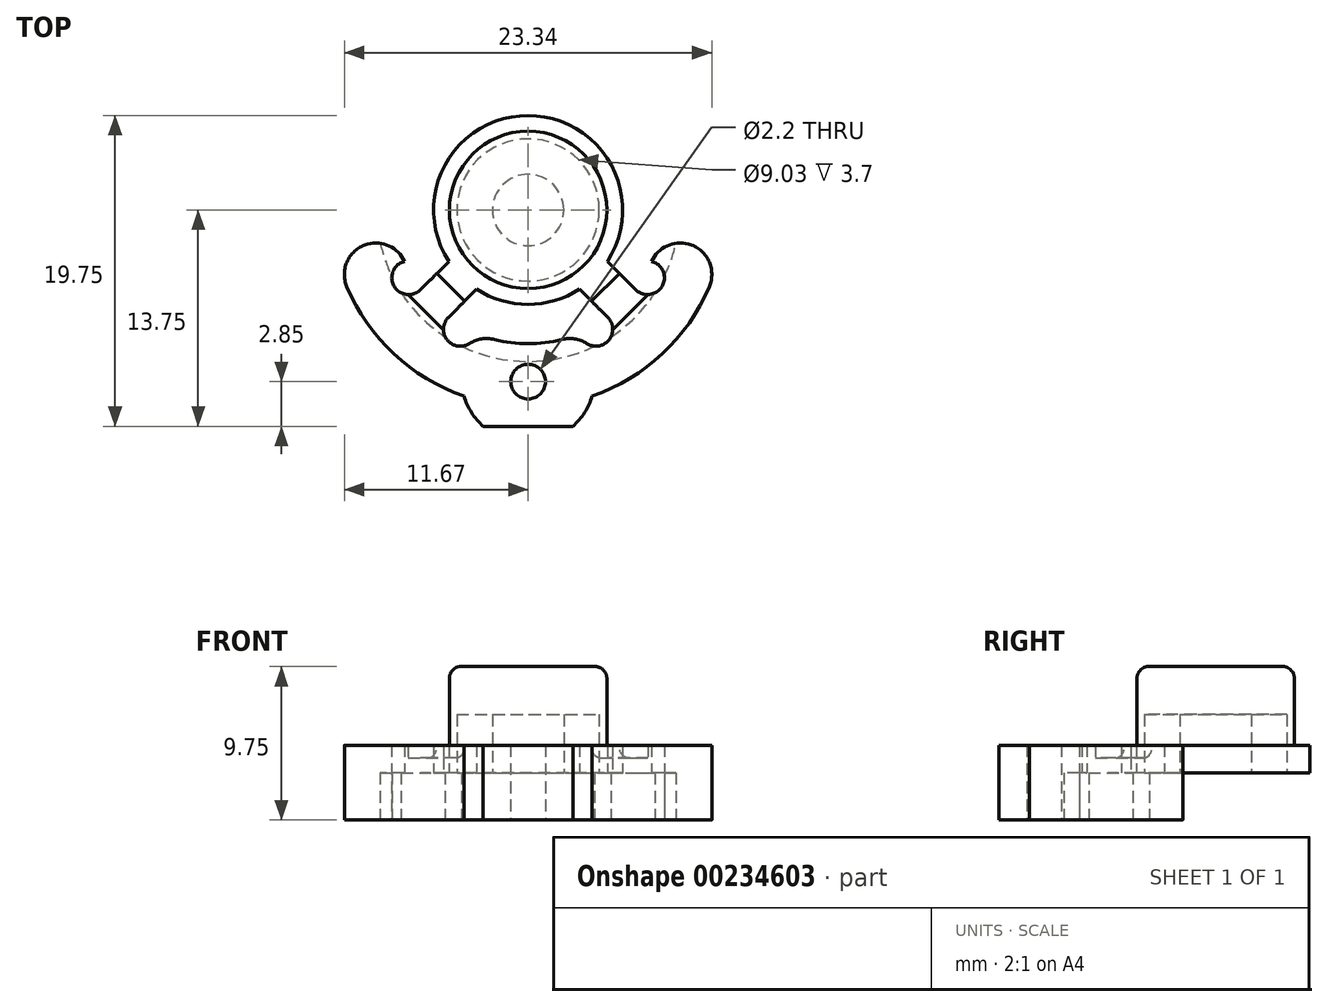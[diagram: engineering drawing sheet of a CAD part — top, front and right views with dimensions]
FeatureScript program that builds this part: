
annotation { "Feature Type Name" : "Feature", "Feature Type Description" : "" }
export const myFeature = defineFeature(function(context is Context, id is Id, definition is map)
    precondition{}
    {
        {
            var Q0;
            Q0=qCreatedBy(makeId("Top.planeOp"),FACE);
            var sketch = newSketch(context, id + "F0", { "sketchPlane" : qUnion([Q0])});
            skLineSegment(sketch, "E0.bottom", {"start": v(4, 3) * mm, "end": v(-4, 3) * mm, "construction": true});
            skLineSegment(sketch, "E0.top", {"start": v(4, -3) * mm, "end": v(-4, -3) * mm, "construction": true});
            skLineSegment(sketch, "E0.left", {"start": v(4, 3) * mm, "end": v(4, -3) * mm, "construction": true});
            skLineSegment(sketch, "E0.right", {"start": v(-4, 3) * mm, "end": v(-4, -3) * mm, "construction": true});
            skPoint(sketch, "E0.middle", {"position": v(0, 0) * mm});
            skArc(sketch, "E1", {"start": v(-12.2, -2.7) * mm, "mid": v(-9.33, -8.32) * mm, "end": v(-4.08, -11.82) * mm});
            skArc(sketch, "E2.converted", {"start": v(-3.27, -5.03) * mm, "mid": v(0, -6) * mm, "end": v(3.27, -5.03) * mm});
            skArc(sketch, "E3", {"start": v(-8.34, -1.67) * mm, "mid": v(-8.13, -2.48) * mm, "end": v(-7.85, -3.27) * mm});
            skPoint(sketch, "E4.orphan", {"position": v(-6, 0) * mm});
            skLineSegment(sketch, "E5", {"start": v(0, 0) * mm, "end": v(14.62, -14.62) * mm, "construction": true});
            skLineSegment(sketch, "E6", {"start": v(5.03, -3.27) * mm, "end": v(6.83, -5.06) * mm});
            skLineSegment(sketch, "E7.MirrorCS", {"start": v(3.27, -5.03) * mm, "end": v(5.06, -6.83) * mm});
            skLineSegment(sketch, "E8.MirrorCS", {"start": v(-5.03, -3.27) * mm, "end": v(-6.83, -5.06) * mm});
            skLineSegment(sketch, "E9.MirrorCS", {"start": v(-3.27, -5.03) * mm, "end": v(-5.06, -6.83) * mm});
            skArc(sketch, "E10", {"start": v(6.83, -5.06) * mm, "mid": v(8.52, -4.83) * mm, "end": v(7.85, -3.27) * mm});
            skArc(sketch, "E11.MirrorCS", {"start": v(5.06, -6.83) * mm, "mid": v(4.83, -8.52) * mm, "end": v(3.27, -7.85) * mm});
            skArc(sketch, "E12.trimOffspring", {"start": v(7.85, -3.27) * mm, "mid": v(8.13, -2.48) * mm, "end": v(8.34, -1.67) * mm});
            skArc(sketch, "E13.MirrorCS", {"start": v(-5.06, -6.83) * mm, "mid": v(-4.83, -8.52) * mm, "end": v(-3.27, -7.85) * mm});
            skArc(sketch, "E14.MirrorCS", {"start": v(-6.83, -5.06) * mm, "mid": v(-8.52, -4.83) * mm, "end": v(-7.85, -3.27) * mm});
            skArc(sketch, "E15.trimOffspring", {"start": v(-3.27, -7.85) * mm, "mid": v(0, -8.5) * mm, "end": v(3.27, -7.85) * mm});
            skArc(sketch, "E16.trimOffspring", {"start": v(5.03, -3.27) * mm, "mid": v(0, 6) * mm, "end": v(-5.03, -3.27) * mm});
            skArc(sketch, "E17.trimOffspring", {"start": v(4.08, -11.82) * mm, "mid": v(9.33, -8.32) * mm, "end": v(12.2, -2.7) * mm});
            skArc(sketch, "E18.trimOffspring", {"start": v(-4.08, -11.82) * mm, "mid": v(-3.6, -12.87) * mm, "end": v(-2.85, -13.75) * mm});
            skCircle(sketch, "E19", {"center": v(0, -10.9) * mm, "radius": 1.1 * mm});
            skLineSegment(sketch, "E20", {"start": v(-8.34, -1.67) * mm, "end": v(-12.2, -2.7) * mm});
            skLineSegment(sketch, "E21.MirrorCS", {"start": v(8.34, -1.67) * mm, "end": v(12.2, -2.7) * mm});
            skPoint(sketch, "E22.orphan", {"position": v(-13.8, -3.13) * mm});
            skPoint(sketch, "E23.orphan", {"position": v(12.5, 0) * mm});
            skPoint(sketch, "E24.orphan", {"position": v(13.8, -3.13) * mm});
            skLineSegment(sketch, "E25", {"start": v(-2.85, -13.75) * mm, "end": v(2.85, -13.75) * mm});
            skArc(sketch, "E26.trimOffspring", {"start": v(2.85, -13.75) * mm, "mid": v(3.6, -12.87) * mm, "end": v(4.08, -11.82) * mm});
            skSolve(sketch);
        }
        {
            var Q0;
            Q0 = qSketchRegion(id + "F0", true);
            extrude(context, id + "F1", {"entities" : qUnion([Q0]), "depth" : 4.75 * mm});
        }
        {
            var Q0;
            Q0=makeQuery(id+"F1.opExtrude","CAP_FACE",FACE,{"disambiguationData":[OSD([sQuery(id+"F0.wireOp",EDGE,"E1"),sQuery(id+"F0.wireOp",EDGE,"E2.converted"),sQuery(id+"F0.wireOp",EDGE,"rdbc6vYB-NVjA-jXWY-TLaR-nZ7SSUkQD9Vy"),sQuery(id+"F0.wireOp",EDGE,"ynKpnGIP-DJsh-uGPF-F4s2-QlGlmaUKXdbb"),sQuery(id+"F0.wireOp",EDGE,"E3"),sQuery(id+"F0.wireOp",EDGE,"E6"),sQuery(id+"F0.wireOp",EDGE,"E7.MirrorCS"),sQuery(id+"F0.wireOp",EDGE,"E8.MirrorCS"),sQuery(id+"F0.wireOp",EDGE,"E9.MirrorCS"),sQuery(id+"F0.wireOp",EDGE,"E10"),sQuery(id+"F0.wireOp",EDGE,"E11.MirrorCS"),sQuery(id+"F0.wireOp",EDGE,"E12.trimOffspring"),sQuery(id+"F0.wireOp",EDGE,"E13.MirrorCS"),sQuery(id+"F0.wireOp",EDGE,"E14.MirrorCS"),sQuery(id+"F0.wireOp",EDGE,"E15.trimOffspring"),sQuery(id+"F0.wireOp",EDGE,"E16.trimOffspring")])],"isStart":false});
            var sketch = newSketch(context, id + "F2", { "sketchPlane" : qUnion([Q0])});
            skCircle(sketch, "E27", {"center": v(0, 0) * mm, "radius": 5 * mm});
            skSolve(sketch);
        }
        {
            var Q0;
            Q0=makeQuery(id+"F2.imprint","IMPRINT",FACE,{"disambiguationData":[TD([[makeQuery(id+"F2.imprint","IMPRINT",EDGE,{"derivedFrom":sQuery(id+"F2.wireOp",EDGE,"E27")}),1.0]])]});
            extrude(context, id + "F3", {"entities" : qUnion([Q0]), "operationType" : NewBodyOperationType.ADD, "depth" : 5 * mm});
        }
        {
            var Q0;
            Q0=makeQuery(id+"F1.opExtrude","CAP_FACE",FACE,{"disambiguationData":[OSD([sQuery(id+"F0.wireOp",EDGE,"E1"),sQuery(id+"F0.wireOp",EDGE,"E2.converted"),sQuery(id+"F0.wireOp",EDGE,"rdbc6vYB-NVjA-jXWY-TLaR-nZ7SSUkQD9Vy"),sQuery(id+"F0.wireOp",EDGE,"ynKpnGIP-DJsh-uGPF-F4s2-QlGlmaUKXdbb"),sQuery(id+"F0.wireOp",EDGE,"E3"),sQuery(id+"F0.wireOp",EDGE,"E6"),sQuery(id+"F0.wireOp",EDGE,"E7.MirrorCS"),sQuery(id+"F0.wireOp",EDGE,"E8.MirrorCS"),sQuery(id+"F0.wireOp",EDGE,"E9.MirrorCS"),sQuery(id+"F0.wireOp",EDGE,"E10"),sQuery(id+"F0.wireOp",EDGE,"E11.MirrorCS"),sQuery(id+"F0.wireOp",EDGE,"E12.trimOffspring"),sQuery(id+"F0.wireOp",EDGE,"E13.MirrorCS"),sQuery(id+"F0.wireOp",EDGE,"E14.MirrorCS"),sQuery(id+"F0.wireOp",EDGE,"E15.trimOffspring"),sQuery(id+"F0.wireOp",EDGE,"E16.trimOffspring")])],"isStart":false});
            var sketch = newSketch(context, id + "F4", { "sketchPlane" : qUnion([Q0])});
            skSolve(sketch);
        }
        {
            var Q0;
            Q0=makeQuery(id+"F1.opExtrude","SWEPT_EDGE",EDGE,{"disambiguationData":[OSD([sQuery(id+"F0.wireOp",EDGE,"E17.trimOffspring"),sQuery(id+"F0.wireOp",EDGE,"E21.MirrorCS")])]});
            var Q1;
            Q1=makeQuery(id+"F1.opExtrude","SWEPT_EDGE",EDGE,{"disambiguationData":[OSD([sQuery(id+"F0.wireOp",EDGE,"E12.trimOffspring"),sQuery(id+"F0.wireOp",EDGE,"E21.MirrorCS")])]});
            var Q2;
            Q2=makeQuery(id+"F1.opExtrude","SWEPT_EDGE",EDGE,{"disambiguationData":[OSD([sQuery(id+"F0.wireOp",EDGE,"E3"),sQuery(id+"F0.wireOp",EDGE,"E20")])]});
            var Q3;
            Q3=makeQuery(id+"F1.opExtrude","SWEPT_EDGE",EDGE,{"disambiguationData":[OSD([sQuery(id+"F0.wireOp",EDGE,"E1"),sQuery(id+"F0.wireOp",EDGE,"E20")])]});
            var Q4;
            Q4=makeQuery(id+"F1.opExtrude","SWEPT_EDGE",EDGE,{"disambiguationData":[OSD([sQuery(id+"F0.wireOp",EDGE,"E11.MirrorCS"),sQuery(id+"F0.wireOp",EDGE,"E15.trimOffspring")])]});
            var Q5;
            Q5=makeQuery(id+"F1.opExtrude","SWEPT_EDGE",EDGE,{"disambiguationData":[OSD([sQuery(id+"F0.wireOp",EDGE,"E13.MirrorCS"),sQuery(id+"F0.wireOp",EDGE,"E15.trimOffspring")])]});
            fillet(context, id + "F5", {"entities" : qUnion([Q0, Q1, Q2, Q3, Q4, Q5]), "radius" : 2 * mm, "tangentPropagation" : true, "allowEdgeOverflow" : false});
        }
        {
            var Q0;
            Q0=makeQuery(id+"F4.imprint","IMPRINT",FACE,{"disambiguationData":[TD([[makeQuery(id+"F4.imprint","IMPRINT",EDGE,{"derivedFrom":makeQuery(id+"F1.opExtrude","CAP_EDGE",EDGE,{"disambiguationData":[OSD([sQuery(id+"F0.wireOp",EDGE,"E1")])],"isStart":false})}),1.0]])]});
            var sketch = newSketch(context, id + "F6", { "sketchPlane" : qUnion([Q0])});
            skLineSegment(sketch, "E28", {"start": v(0, 0) * mm, "end": v(16.52, -16.52) * mm, "construction": true});
            skLineSegment(sketch, "E29", {"start": v(8.62, -4.38) * mm, "end": v(4.38, -8.62) * mm});
            skLineSegment(sketch, "E30", {"start": v(4.38, -8.62) * mm, "end": v(2.79, -7.03) * mm});
            skLineSegment(sketch, "E31", {"start": v(2.79, -7.03) * mm, "end": v(7, -2.8) * mm});
            skLineSegment(sketch, "E32", {"start": v(7, -2.8) * mm, "end": v(8.62, -4.38) * mm});
            skLineSegment(sketch, "E33.MirrorCS", {"start": v(-2.79, -7.03) * mm, "end": v(-7, -2.8) * mm});
            skLineSegment(sketch, "E34.MirrorCS", {"start": v(-7, -2.8) * mm, "end": v(-8.62, -4.38) * mm});
            skLineSegment(sketch, "E35.MirrorCS", {"start": v(-8.62, -4.38) * mm, "end": v(-4.38, -8.62) * mm});
            skLineSegment(sketch, "E36.MirrorCS", {"start": v(-4.38, -8.62) * mm, "end": v(-2.79, -7.03) * mm});
            skSolve(sketch);
        }
        {
            var Q0;
            Q0 = qSketchRegion(id + "F6", true);
            extrude(context, id + "F7", {"entities" : qUnion([Q0]), "operationType" : NewBodyOperationType.REMOVE, "oppositeDirection" : true, "depth" : .8 * mm});
        }
        {
            var Q0;
            Q0=makeQuery(id+"F7.boolean.opBoolean","COPY",EDGE,{"derivedFrom":makeQuery(id+"F7.opExtrude","CAP_EDGE",EDGE,{"disambiguationData":[OSD([sQuery(id+"F6.wireOp",EDGE,"E31")])],"isStart":false})});
            var Q1;
            Q1=makeQuery(id+"F7.boolean.opBoolean","COPY",EDGE,{"derivedFrom":makeQuery(id+"F7.opExtrude","CAP_EDGE",EDGE,{"disambiguationData":[OSD([sQuery(id+"F6.wireOp",EDGE,"E33.MirrorCS")])],"isStart":false})});
            var Q2;
            Q2=makeQuery(id+"F3.opExtrude","CAP_EDGE",EDGE,{"disambiguationData":[OSD([sQuery(id+"F2.wireOp",EDGE,"E27")])],"isStart":true});
            var Q3;
            Q3=makeQuery(id+"F3.opExtrude","CAP_EDGE",EDGE,{"disambiguationData":[OSD([sQuery(id+"F2.wireOp",EDGE,"E27")])],"isStart":false});
            fillet(context, id + "F8", {"entities" : qUnion([Q0, Q1, Q2, Q3]), "radius" : .75 * mm, "tangentPropagation" : true, "allowEdgeOverflow" : false});
        }
        {
            var Q0;
            Q0=qCreatedBy(makeId("Top.planeOp"),FACE);
            var sketch = newSketch(context, id + "F9", { "sketchPlane" : qUnion([Q0])});
            skCircle(sketch, "E37", {"center": v(0, 0) * mm, "radius": 9.62 * mm});
            skSolve(sketch);
        }
        {
            var Q0;
            Q0 = qSketchRegion(id + "F9", true);
            extrude(context, id + "F10", {"entities" : qUnion([Q0]), "operationType" : NewBodyOperationType.REMOVE, "depth" : 3 * mm});
        }
        {
            var Q0;
            {var subQ0=sQuery(id+"F9.wireOp",EDGE,"E37");Q0=makeQuery(id+"F10.boolean.opBoolean","COPY",FACE,{"disambiguationData":[TD([makeQuery(id+"F1.opExtrude","SWEPT_FACE",FACE,{"disambiguationData":[OSD([sQuery(id+"F0.wireOp",EDGE,"E2.converted")])]})])],"derivedFrom":makeQuery(id+"F10.opExtrude","CAP_FACE",FACE,{"disambiguationData":[OSD([subQ0])],"isStart":false})});}
            var sketch = newSketch(context, id + "F11", { "sketchPlane" : qUnion([Q0])});
            skCircle(sketch, "E38", {"center": v(0, 0) * mm, "radius": 2 * mm});
            skSolve(sketch);
        }
        {
            var Q0;
            {var subQ0=sQuery(id+"F9.wireOp",EDGE,"E37");Q0=makeQuery(id+"F10.boolean.opBoolean","COPY",FACE,{"disambiguationData":[TD([makeQuery(id+"F1.opExtrude","SWEPT_FACE",FACE,{"disambiguationData":[OSD([sQuery(id+"F0.wireOp",EDGE,"E2.converted")])]})])],"derivedFrom":makeQuery(id+"F10.opExtrude","CAP_FACE",FACE,{"disambiguationData":[OSD([subQ0])],"isStart":false})});}
            var sketch = newSketch(context, id + "F12", { "sketchPlane" : qUnion([Q0])});
            skCircle(sketch, "E39", {"center": v(0, 0) * mm, "radius": 4.52 * mm});
            skCircle(sketch, "E40", {"center": v(0, 0) * mm, "radius": 2.27 * mm});
            skSolve(sketch);
        }
        {
            var Q0;
            Q0 = qSketchRegion(id + "F12", true);
            extrude(context, id + "F13", {"entities" : qUnion([Q0]), "operationType" : NewBodyOperationType.REMOVE, "oppositeDirection" : true, "depth" : 3.7 * mm});
        }
    });
